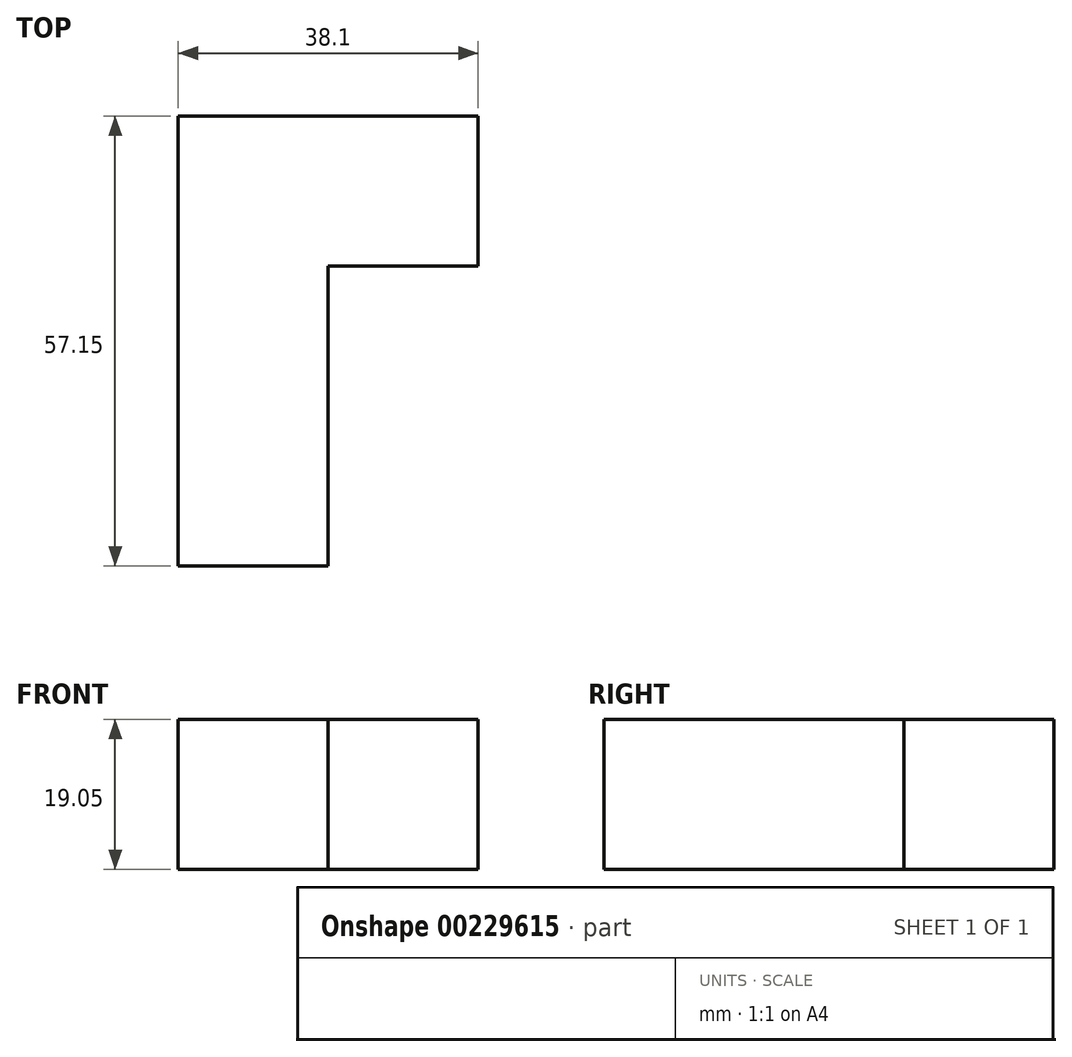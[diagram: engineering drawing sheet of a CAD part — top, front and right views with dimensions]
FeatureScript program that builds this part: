
annotation { "Feature Type Name" : "Feature", "Feature Type Description" : "" }
export const myFeature = defineFeature(function(context is Context, id is Id, definition is map)
    precondition{}
    {
        {
            var Q0;
            Q0=qCreatedBy(makeId("Top.planeOp"),FACE);
            var sketch = newSketch(context, id + "F0", { "sketchPlane" : qUnion([Q0])});
            skLineSegment(sketch, "E0", {"start": v(0, 0) * mm, "end": v(0, 57.15) * mm});
            skLineSegment(sketch, "E1", {"start": v(0, 57.15) * mm, "end": v(19.05, 57.15) * mm});
            skLineSegment(sketch, "E2", {"start": v(0, 0) * mm, "end": v(19.05, 0) * mm});
            skLineSegment(sketch, "E3", {"start": v(19.05, 0) * mm, "end": v(19.05, 38.1) * mm});
            skLineSegment(sketch, "E4", {"start": v(19.05, 38.1) * mm, "end": v(38.1, 38.1) * mm});
            skLineSegment(sketch, "E5", {"start": v(19.05, 57.15) * mm, "end": v(38.1, 57.15) * mm});
            skLineSegment(sketch, "E6", {"start": v(38.1, 57.15) * mm, "end": v(38.1, 38.1) * mm});
            skSolve(sketch);
        }
        {
            var Q0;
            Q0=makeQuery(id+"F0.imprint","IMPRINT",FACE,{"disambiguationData":[TD([[makeQuery(id+"F0.imprint","IMPRINT",EDGE,{"derivedFrom":sQuery(id+"F0.wireOp",EDGE,"E0")}),-1.0]])]});
            extrude(context, id + "F1", {"entities" : qUnion([Q0]), "depth" : 19.05 * mm});
        }
    });
